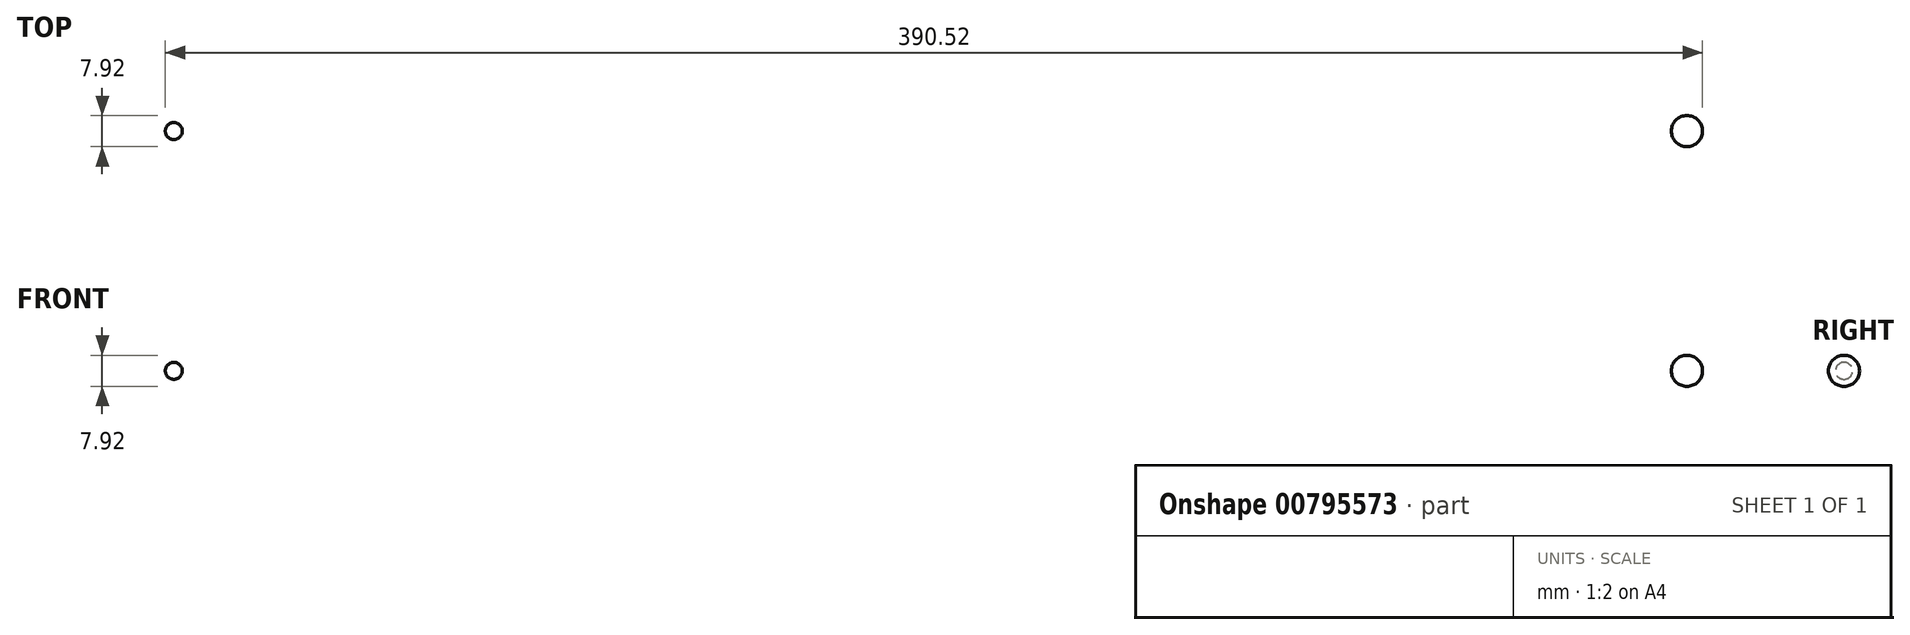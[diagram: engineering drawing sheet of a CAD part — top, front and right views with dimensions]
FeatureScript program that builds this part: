
annotation { "Feature Type Name" : "Feature", "Feature Type Description" : "" }
export const myFeature = defineFeature(function(context is Context, id is Id, definition is map)
    precondition{}
    {
        {
            var Q0;
            Q0=qCreatedBy(makeId("Front.planeOp"),FACE);
            var sketch = newSketch(context, id + "F0", { "sketchPlane" : qUnion([Q0])});
            skArc(sketch, "E0", {"start": v(0, -3.96) * mm, "mid": v(3.96, 0) * mm, "end": v(0, 3.96) * mm});
            skLineSegment(sketch, "E1", {"start": v(0, 3.96) * mm, "end": v(0, -3.96) * mm, "construction": true});
            skLineSegment(sketch, "E2", {"start": v(0, 0) * mm, "end": v(-384.4, 0) * mm, "construction": true});
            skArc(sketch, "E3", {"start": v(-384.4, 2.16) * mm, "mid": v(-386.56, 0) * mm, "end": v(-384.4, -2.16) * mm});
            skLineSegment(sketch, "E4", {"start": v(-384.4, -2.16) * mm, "end": v(-384.4, 2.16) * mm, "construction": true});
            skSolve(sketch);
        }
        {
            var Q0;
            Q0=makeQuery(id+"F0.imprint","IMPRINT",FACE,{"disambiguationData":[TD([[makeQuery(id+"F0.imprint","IMPRINT",EDGE,{"derivedFrom":sQuery(id+"F0.wireOp",EDGE,"E0")}),1.0]])]});
            var Q1;
            Q1=sQuery(id+"F0.wireOp",EDGE,"E0");
            var Q2;
            Q2=sQuery(id+"F0.wireOp",EDGE,"E1");
            revolve(context, id + "F1", {"bodyType" : ToolBodyType.SURFACE, "surfaceOperationType" : NewSurfaceOperationType.NEW, "entities" : qUnion([Q0]), "surfaceEntities" : qUnion([Q1]), "axis" : qUnion([Q2]), "revolveType" : RevolveType.FULL});
        }
        {
            var Q0;
            Q0=sQuery(id+"F0.wireOp",EDGE,"E3");
            var Q1;
            Q1=sQuery(id+"F0.wireOp",EDGE,"E4");
            revolve(context, id + "F2", {"bodyType" : ToolBodyType.SURFACE, "surfaceOperationType" : NewSurfaceOperationType.NEW, "surfaceEntities" : qUnion([Q0]), "axis" : qUnion([Q1]), "revolveType" : RevolveType.FULL});
        }
    });
